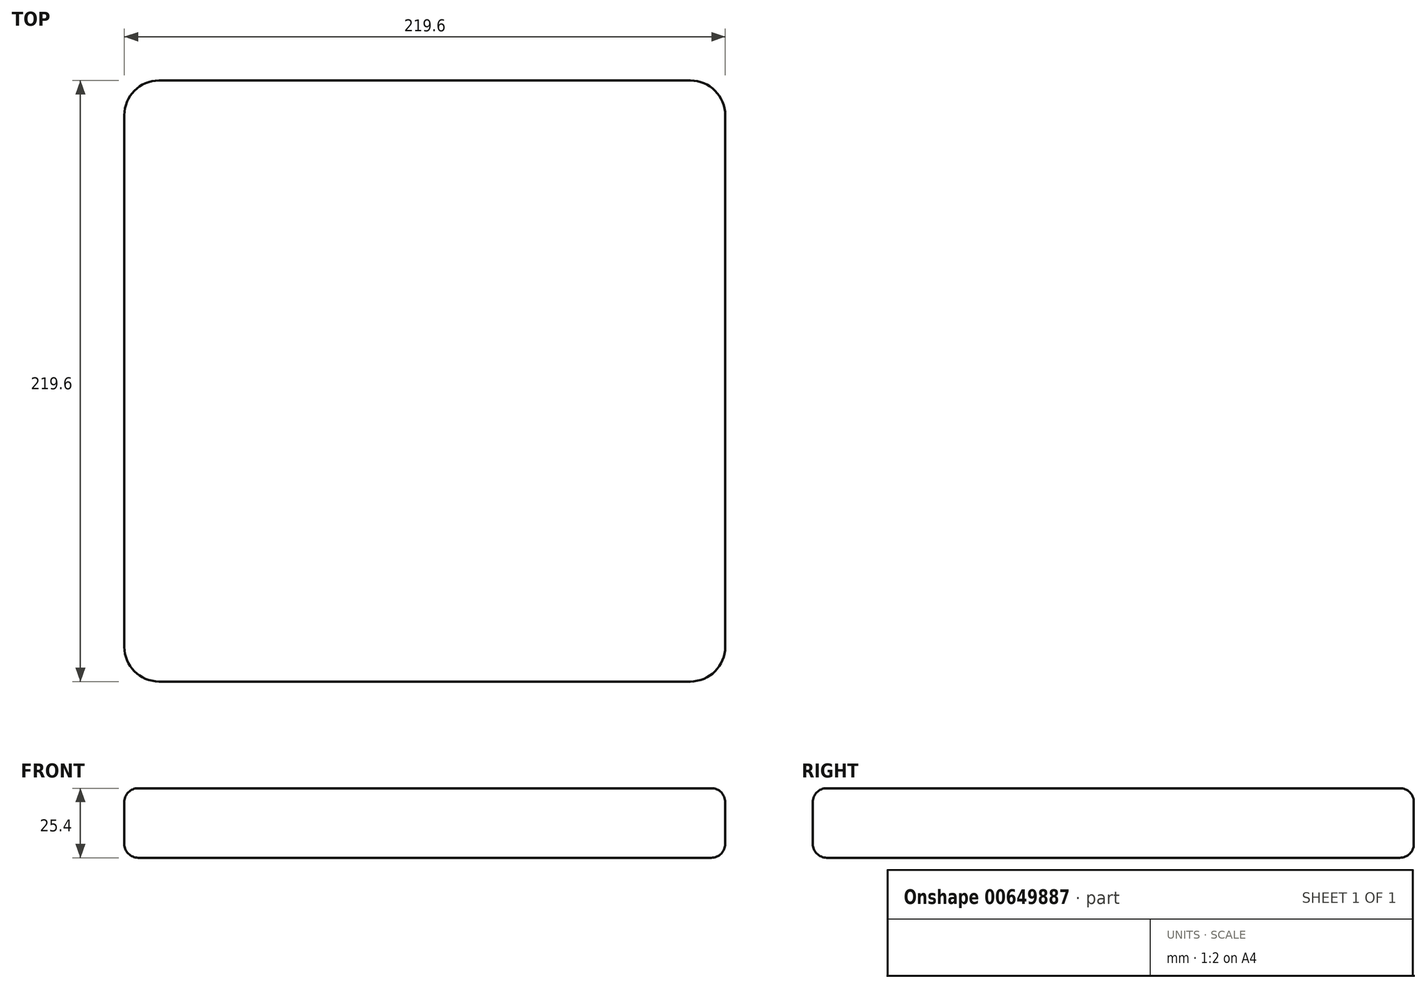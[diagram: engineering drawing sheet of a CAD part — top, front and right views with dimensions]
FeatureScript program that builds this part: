
annotation { "Feature Type Name" : "Feature", "Feature Type Description" : "" }
export const myFeature = defineFeature(function(context is Context, id is Id, definition is map)
    precondition{}
    {
        {
            var Q0;
            Q0=qCreatedBy(makeId("Top.planeOp"),FACE);
            var sketch = newSketch(context, id + "F0", { "sketchPlane" : qUnion([Q0])});
            skLineSegment(sketch, "E0.bottom", {"start": v(-109.8, -109.8) * mm, "end": v(109.8, -109.8) * mm});
            skLineSegment(sketch, "E0.top", {"start": v(-109.8, 109.8) * mm, "end": v(109.8, 109.8) * mm});
            skLineSegment(sketch, "E0.left", {"start": v(-109.8, -109.8) * mm, "end": v(-109.8, 109.8) * mm});
            skLineSegment(sketch, "E0.right", {"start": v(109.8, -109.8) * mm, "end": v(109.8, 109.8) * mm});
            skPoint(sketch, "E0.middle", {"position": v(0, 0) * mm});
            skSolve(sketch);
        }
        {
            var Q0;
            Q0=makeQuery(id+"F0.imprint","IMPRINT",FACE,{"disambiguationData":[TD([[makeQuery(id+"F0.imprint","IMPRINT",EDGE,{"derivedFrom":sQuery(id+"F0.wireOp",EDGE,"E0.bottom")}),1.0]])]});
            extrude(context, id + "F1", {"entities" : qUnion([Q0]), "depth" : 25.4 * mm, "offsetDistance" : 25.4 * mm});
        }
        {
            var Q0;
            Q0=makeQuery(id+"F1.opExtrude","SWEPT_EDGE",EDGE,{"disambiguationData":[OSD([sQuery(id+"F0.wireOp",EDGE,"E0.bottom"),sQuery(id+"F0.wireOp",EDGE,"E0.right")])]});
            var Q1;
            Q1=makeQuery(id+"F1.opExtrude","SWEPT_EDGE",EDGE,{"disambiguationData":[OSD([sQuery(id+"F0.wireOp",EDGE,"E0.top"),sQuery(id+"F0.wireOp",EDGE,"E0.right")])]});
            var Q2;
            Q2=makeQuery(id+"F1.opExtrude","SWEPT_EDGE",EDGE,{"disambiguationData":[OSD([sQuery(id+"F0.wireOp",EDGE,"E0.bottom"),sQuery(id+"F0.wireOp",EDGE,"E0.left")])]});
            var Q3;
            Q3=makeQuery(id+"F1.opExtrude","SWEPT_EDGE",EDGE,{"disambiguationData":[OSD([sQuery(id+"F0.wireOp",EDGE,"E0.top"),sQuery(id+"F0.wireOp",EDGE,"E0.left")])]});
            fillet(context, id + "F2", {"entities" : qUnion([Q0, Q1, Q2, Q3]), "radius" : 12.7 * mm, "tangentPropagation" : true, "allowEdgeOverflow" : false});
        }
        {
            var Q0;
            Q0=makeQuery(id+"F1.opExtrude","CAP_FACE",FACE,{"disambiguationData":[OSD([sQuery(id+"F0.wireOp",EDGE,"E0.bottom"),sQuery(id+"F0.wireOp",EDGE,"E0.top"),sQuery(id+"F0.wireOp",EDGE,"E0.left"),sQuery(id+"F0.wireOp",EDGE,"E0.right")])],"isStart":false});
            var Q1;
            Q1=makeQuery(id+"F1.opExtrude","CAP_FACE",FACE,{"disambiguationData":[OSD([sQuery(id+"F0.wireOp",EDGE,"E0.bottom"),sQuery(id+"F0.wireOp",EDGE,"E0.top"),sQuery(id+"F0.wireOp",EDGE,"E0.left"),sQuery(id+"F0.wireOp",EDGE,"E0.right")])],"isStart":true});
            fillet(context, id + "F3", {"entities" : qUnion([Q0, Q1]), "radius" : 5.08 * mm, "tangentPropagation" : true, "allowEdgeOverflow" : false});
        }
    });
